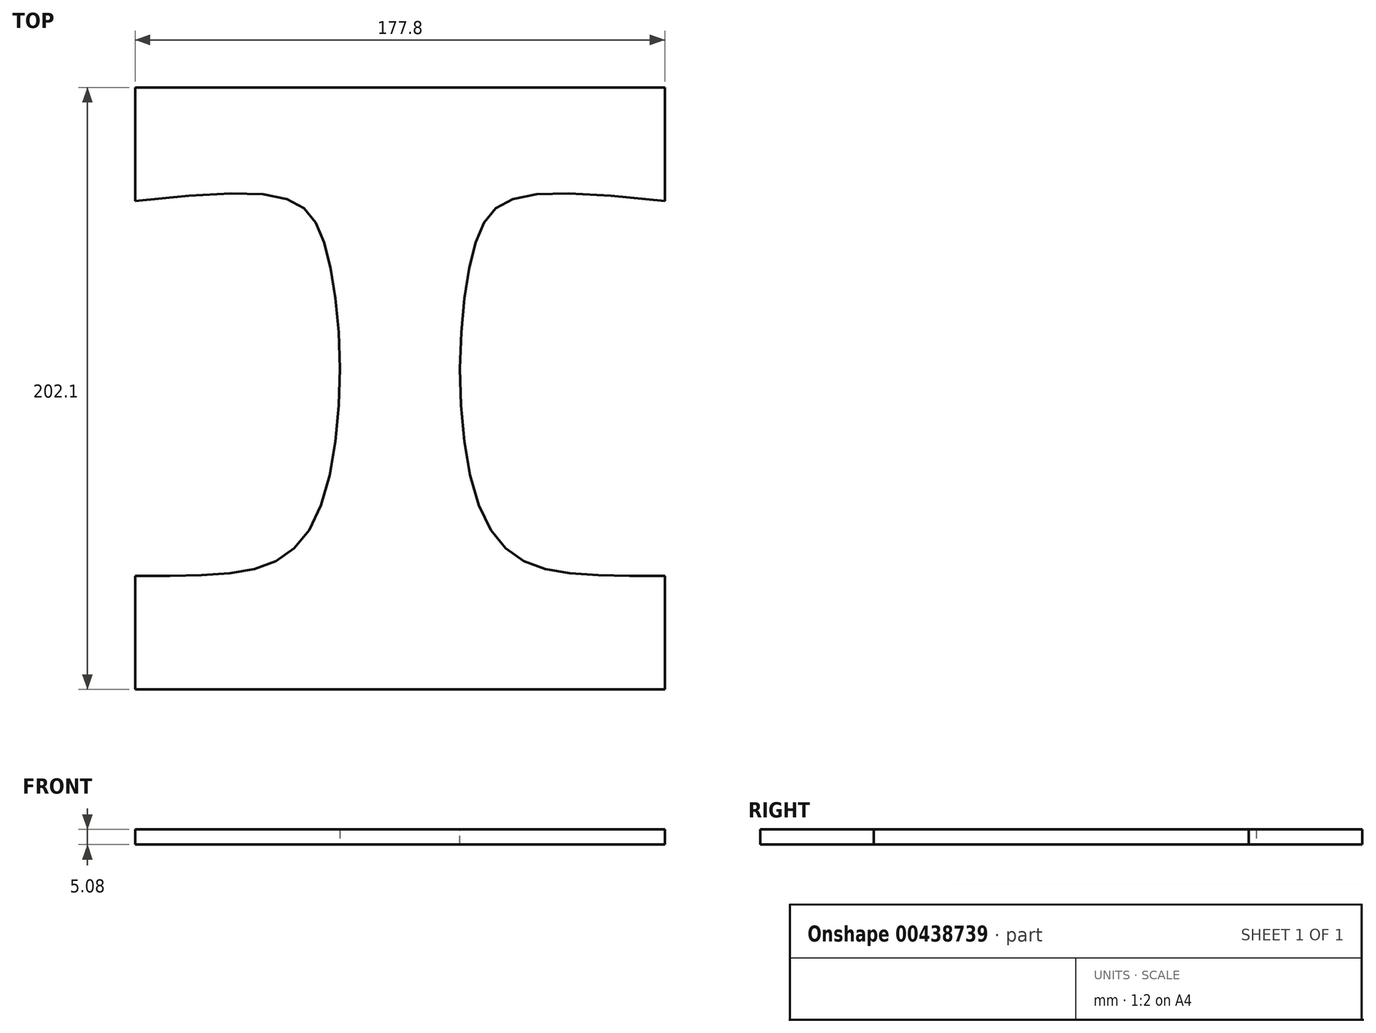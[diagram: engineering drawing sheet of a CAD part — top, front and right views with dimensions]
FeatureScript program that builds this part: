
annotation { "Feature Type Name" : "Feature", "Feature Type Description" : "" }
export const myFeature = defineFeature(function(context is Context, id is Id, definition is map)
    precondition{}
    {
        {
            var Q0;
            Q0=qCreatedBy(makeId("Top.planeOp"),FACE);
            var sketch = newSketch(context, id + "F0", { "sketchPlane" : qUnion([Q0])});
            skLineSegment(sketch, "E0", {"start": v(0, 108.57) * mm, "end": v(88.9, 108.57) * mm});
            skLineSegment(sketch, "E1", {"start": v(88.9, 108.57) * mm, "end": v(88.9, 70.47) * mm});
            skFitSpline(sketch, "E2", {"points": [v(88.9, 70.47) * mm, v(24.72, 54.3) * mm, v(30.63, -40.26) * mm, v(88.9, -55.43) * mm], "startDerivative": vector(-464.17, 50) * mm, "endDerivative": vector(283.47, -3.1) * mm});
            skLineSegment(sketch, "E3", {"start": v(88.9, -55.43) * mm, "end": v(88.9, -93.53) * mm});
            skLineSegment(sketch, "E4", {"start": v(88.9, -93.53) * mm, "end": v(0, -93.53) * mm});
            skLineSegment(sketch, "E5", {"start": v(0, 169.34) * mm, "end": v(0, -123.9) * mm, "construction": true});
            skLineSegment(sketch, "E6.MirrorCS", {"start": v(-88.9, 108.57) * mm, "end": v(-88.9, 70.47) * mm});
            skLineSegment(sketch, "E7.MirrorCS", {"start": v(-88.9, -93.53) * mm, "end": v(0, -93.53) * mm});
            skLineSegment(sketch, "E8.MirrorCS", {"start": v(0, 108.57) * mm, "end": v(-88.9, 108.57) * mm});
            skFitSpline(sketch, "E9.MirrorCS", {"points": [v(-88.9, 70.47) * mm, v(-24.72, 54.3) * mm, v(-30.63, -40.26) * mm, v(-88.9, -55.43) * mm], "startDerivative": vector(464.17, 50) * mm, "endDerivative": vector(-283.47, -3.1) * mm});
            skLineSegment(sketch, "E10.MirrorCS", {"start": v(-88.9, -55.43) * mm, "end": v(-88.9, -93.53) * mm});
            skPoint(sketch, "E11", {"position": v(-20.2, 10.42) * mm});
            skPoint(sketch, "E12", {"position": v(20.2, 10.42) * mm});
            skSolve(sketch);
        }
        {
            var Q0;
            Q0 = qSketchRegion(id + "F0", true);
            var Q1;
            Q1=sQuery(id+"F0.wireOp",EDGE,"d1fd69b8-5e67-4ef9-aa2b-214c4c974c915.MirrorCS");
            extrude(context, id + "F1", {"entities" : qUnion([Q0]), "surfaceEntities" : qUnion([Q1]), "depth" : 5.08 * mm});
        }
    });
